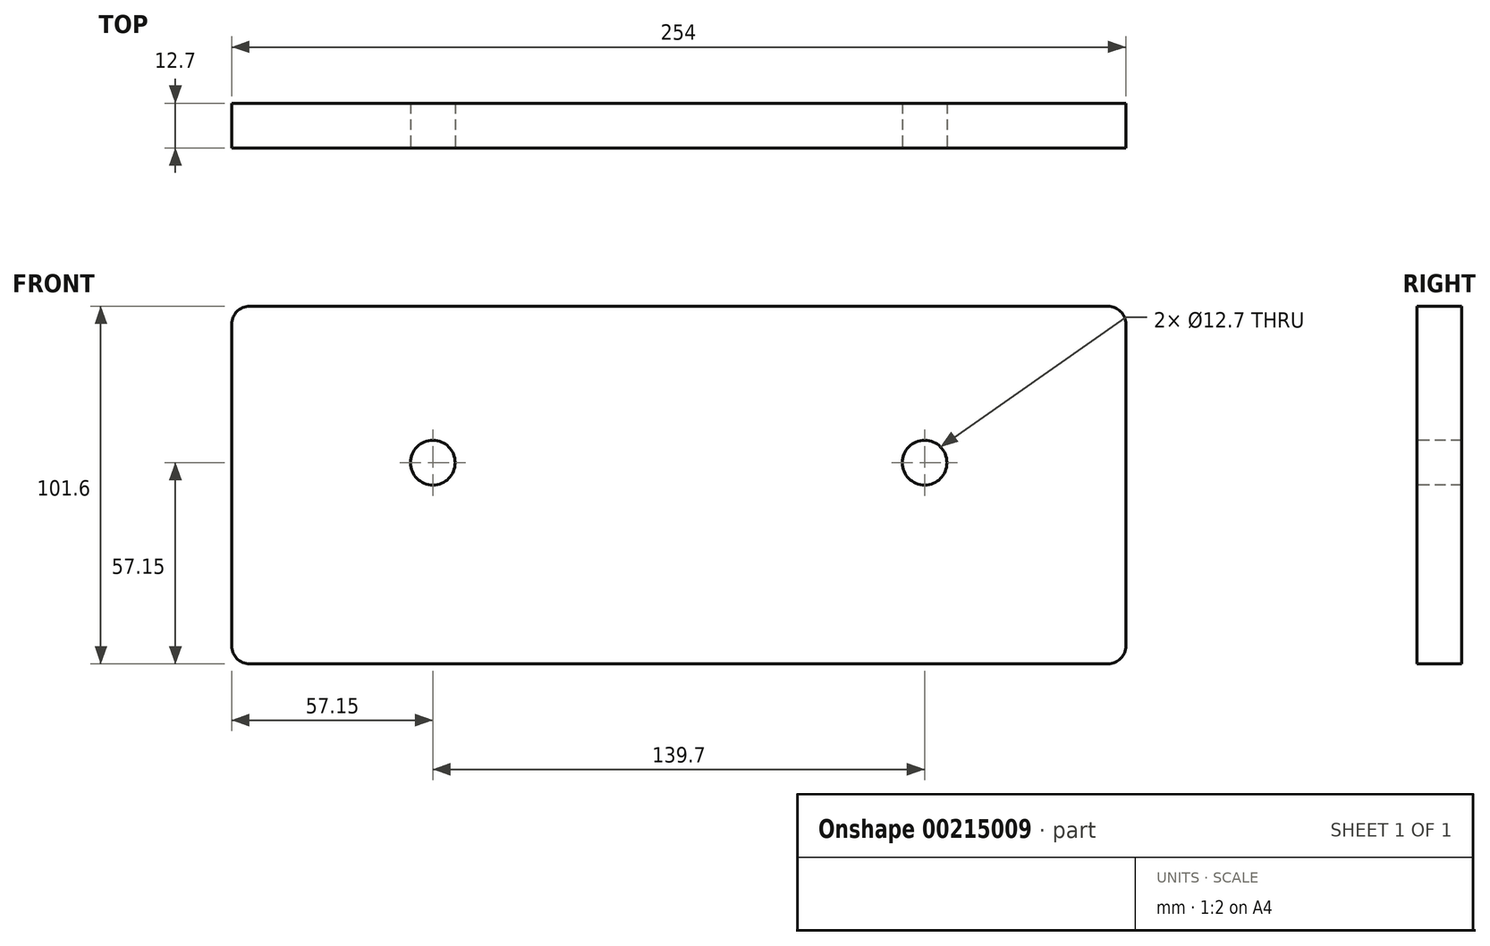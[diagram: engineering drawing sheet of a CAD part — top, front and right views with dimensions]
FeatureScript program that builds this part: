
annotation { "Feature Type Name" : "Feature", "Feature Type Description" : "" }
export const myFeature = defineFeature(function(context is Context, id is Id, definition is map)
    precondition{}
    {
        {
            var Q0;
            Q0=qCreatedBy(makeId("Front.planeOp"),FACE);
            var sketch = newSketch(context, id + "F0", { "sketchPlane" : qUnion([Q0])});
            skLineSegment(sketch, "E0.bottom", {"start": v(0, 0) * mm, "end": v(254, 0) * mm});
            skLineSegment(sketch, "E0.top", {"start": v(0, 101.6) * mm, "end": v(254, 101.6) * mm});
            skLineSegment(sketch, "E0.left", {"start": v(0, 0) * mm, "end": v(0, 101.6) * mm});
            skLineSegment(sketch, "E0.right", {"start": v(254, 0) * mm, "end": v(254, 101.6) * mm});
            skSolve(sketch);
        }
        {
            var Q0;
            Q0 = qSketchRegion(id + "F0", true);
            extrude(context, id + "F1", {"entities" : qUnion([Q0]), "depth" : 12.7 * mm});
        }
        {
            var Q0;
            Q0=makeQuery(id+"F1.opExtrude","CAP_FACE",FACE,{"disambiguationData":[OSD([sQuery(id+"F0.wireOp",EDGE,"E0.bottom"),sQuery(id+"F0.wireOp",EDGE,"E0.top"),sQuery(id+"F0.wireOp",EDGE,"E0.left"),sQuery(id+"F0.wireOp",EDGE,"E0.right")])],"isStart":false});
            var sketch = newSketch(context, id + "F2", { "sketchPlane" : qUnion([Q0])});
            skCircle(sketch, "E1", {"center": v(57.15, 57.15) * mm, "radius": 6.35 * mm});
            skCircle(sketch, "E2", {"center": v(196.85, 57.15) * mm, "radius": 6.35 * mm});
            skSolve(sketch);
        }
        {
            var Q0;
            Q0=sQuery(id+"F2.wireOp",VERTEX,"E1.center");
            var Q1;
            Q1=sQuery(id+"F2.wireOp",VERTEX,"E2.center");
            var Q2;
            Q2=makeQuery(id+"F1.opExtrude","SWEPT_BODY",BODY,{"disambiguationData":[OSD([sQuery(id+"F0.wireOp",EDGE,"E0.bottom"),sQuery(id+"F0.wireOp",EDGE,"E0.top"),sQuery(id+"F0.wireOp",EDGE,"E0.left"),sQuery(id+"F0.wireOp",EDGE,"E0.right")])]});
            hole(context, id + "F3", {"style" : HoleStyle.SIMPLE, "endStyle" : HoleEndStyle.THROUGH, "holeDiameter" : 12.7 * mm, "isTappedThrough" : true, "tappedDepth" : 12.7 * mm, "tapClearance" : 3, "locations" : qUnion([Q0, Q1]), "scope" : qUnion([Q2])});
        }
        {
            var Q0;
            Q0=makeQuery(id+"F1.opExtrude","SWEPT_EDGE",EDGE,{"disambiguationData":[OSD([sQuery(id+"F0.wireOp",EDGE,"E0.top"),sQuery(id+"F0.wireOp",EDGE,"E0.right")])]});
            var Q1;
            Q1=makeQuery(id+"F1.opExtrude","SWEPT_EDGE",EDGE,{"disambiguationData":[OSD([sQuery(id+"F0.wireOp",EDGE,"E0.bottom"),sQuery(id+"F0.wireOp",EDGE,"E0.right")])]});
            var Q2;
            Q2=makeQuery(id+"F1.opExtrude","SWEPT_EDGE",EDGE,{"disambiguationData":[OSD([sQuery(id+"F0.wireOp",EDGE,"E0.bottom"),sQuery(id+"F0.wireOp",EDGE,"E0.left")])]});
            var Q3;
            Q3=makeQuery(id+"F1.opExtrude","SWEPT_EDGE",EDGE,{"disambiguationData":[OSD([sQuery(id+"F0.wireOp",EDGE,"E0.top"),sQuery(id+"F0.wireOp",EDGE,"E0.left")])]});
            fillet(context, id + "F4", {"entities" : qUnion([Q0, Q1, Q2, Q3]), "radius" : 5.08 * mm, "tangentPropagation" : true, "allowEdgeOverflow" : false});
        }
    });
